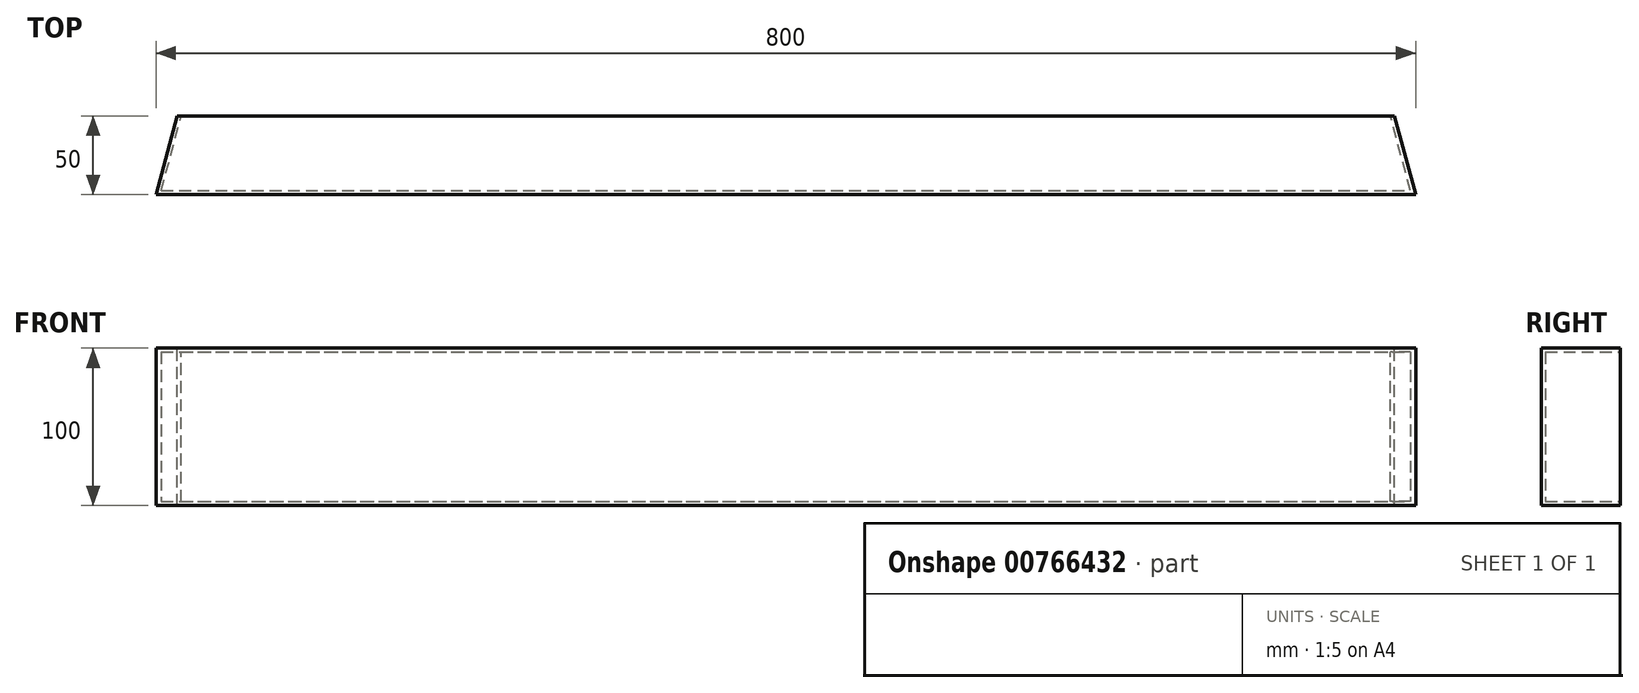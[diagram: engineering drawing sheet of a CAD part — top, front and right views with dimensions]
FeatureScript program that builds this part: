
annotation { "Feature Type Name" : "Feature", "Feature Type Description" : "" }
export const myFeature = defineFeature(function(context is Context, id is Id, definition is map)
    precondition{}
    {
        {
            var Q0;
            Q0=qCreatedBy(makeId("Front.planeOp"),FACE);
            var sketch = newSketch(context, id + "F0", { "sketchPlane" : qUnion([Q0])});
            skLineSegment(sketch, "E0.bottom", {"start": v(-62.11, 51.86) * mm, "end": v(737.89, 51.86) * mm});
            skLineSegment(sketch, "E0.top", {"start": v(-62.11, -48.14) * mm, "end": v(737.89, -48.14) * mm});
            skLineSegment(sketch, "E0.left", {"start": v(-62.11, 51.86) * mm, "end": v(-62.11, -48.14) * mm});
            skLineSegment(sketch, "E0.right", {"start": v(737.89, 51.86) * mm, "end": v(737.89, -48.14) * mm});
            skSolve(sketch);
        }
        {
            var Q0;
            Q0 = qSketchRegion(id + "F0", true);
            extrude(context, id + "F1", {"entities" : qUnion([Q0]), "depth" : 50 * mm, "offsetDistance" : 25 * mm});
        }
        {
            var Q0;
            Q0=makeQuery(id+"F1.opExtrude","SWEPT_FACE",FACE,{"disambiguationData":[OSD([sQuery(id+"F0.wireOp",EDGE,"E0.bottom")])]});
            var sketch = newSketch(context, id + "F2", { "sketchPlane" : qUnion([Q0])});
            skLineSegment(sketch, "E1", {"start": v(-62.11, -50) * mm, "end": v(-36.07, 47.2) * mm});
            skLineSegment(sketch, "E2", {"start": v(-36.07, 47.2) * mm, "end": v(-99.16, 0) * mm});
            skLineSegment(sketch, "E3", {"start": v(-99.16, 0) * mm, "end": v(-90.43, -71.46) * mm});
            skLineSegment(sketch, "E4", {"start": v(-90.43, -71.46) * mm, "end": v(-61.94, -52) * mm});
            skLineSegment(sketch, "E5", {"start": v(-61.94, -52) * mm, "end": v(-62.11, -50) * mm});
            skLineSegment(sketch, "E6", {"start": v(737.89, -50) * mm, "end": v(713.15, 42.31) * mm});
            skLineSegment(sketch, "E7", {"start": v(713.15, 42.31) * mm, "end": v(814.01, 33.62) * mm});
            skLineSegment(sketch, "E8", {"start": v(814.01, 33.62) * mm, "end": v(805.34, -50.86) * mm});
            skLineSegment(sketch, "E9", {"start": v(805.34, -50.86) * mm, "end": v(737.89, -50) * mm});
            skSolve(sketch);
        }
        {
            var Q0;
            Q0 = qSketchRegion(id + "F2", true);
            extrude(context, id + "F3", {"entities" : qUnion([Q0]), "operationType" : NewBodyOperationType.REMOVE, "endBound" : BoundingType.THROUGH_ALL, "oppositeDirection" : true, "depth" : 25 * mm, "offsetDistance" : 25 * mm});
        }
        {
            var Q0;
            Q0=makeQuery(id+"F1.opExtrude","CAP_FACE",FACE,{"disambiguationData":[OSD([sQuery(id+"F0.wireOp",EDGE,"E0.bottom"),sQuery(id+"F0.wireOp",EDGE,"E0.top"),sQuery(id+"F0.wireOp",EDGE,"E0.left"),sQuery(id+"F0.wireOp",EDGE,"E0.right")])],"isStart":true});
            shell(context, id + "F4", {"entities" : qUnion([Q0]), "thickness" : 2.5 * mm});
        }
    });
